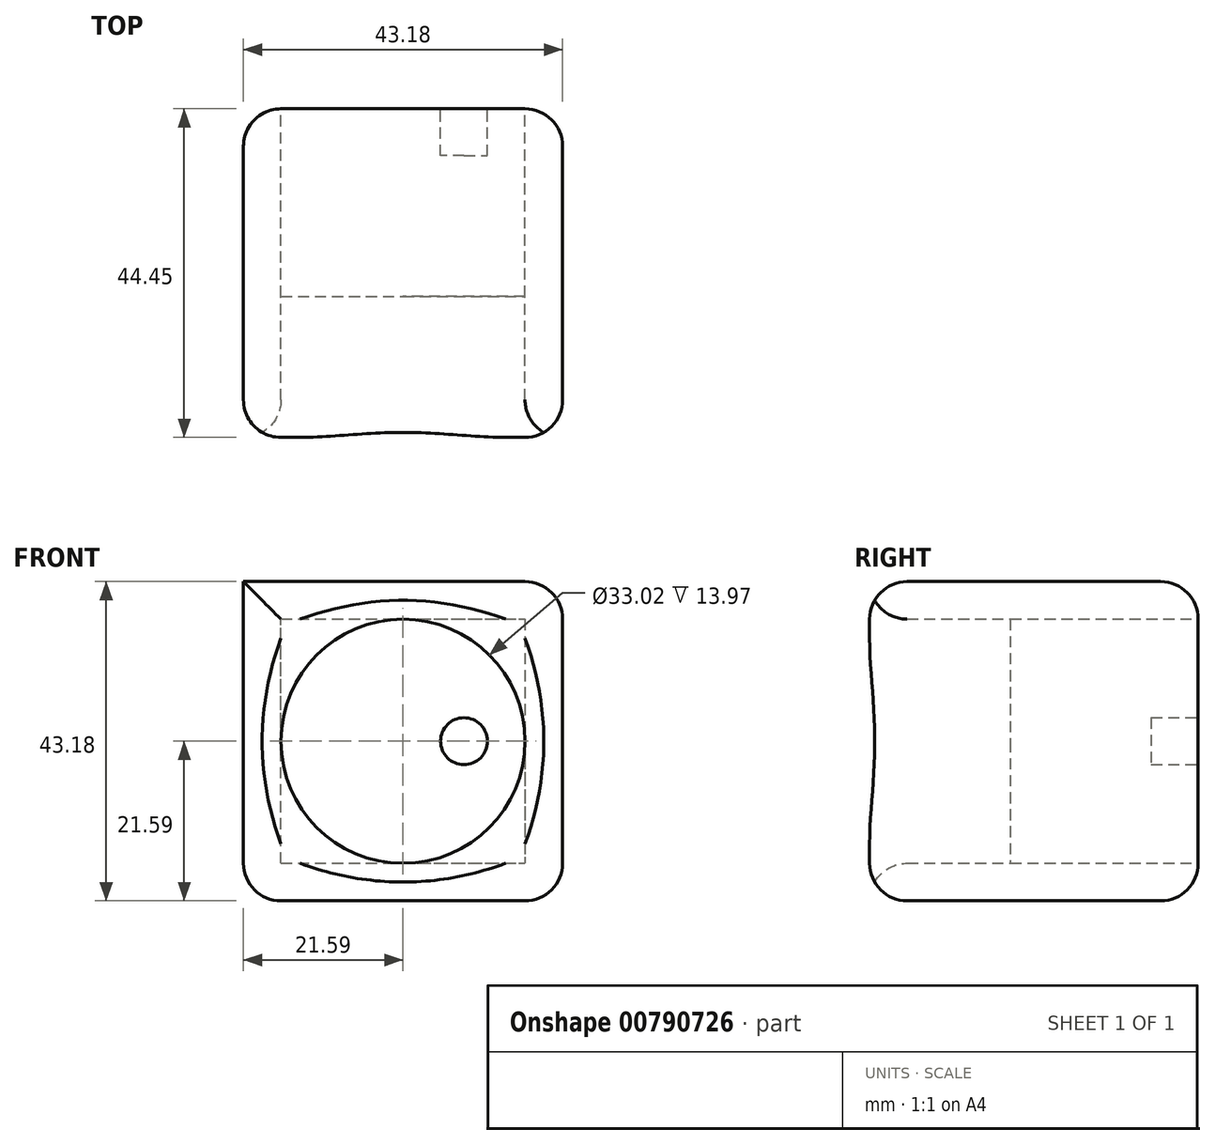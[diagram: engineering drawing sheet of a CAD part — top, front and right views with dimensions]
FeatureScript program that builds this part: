
annotation { "Feature Type Name" : "Feature", "Feature Type Description" : "" }
export const myFeature = defineFeature(function(context is Context, id is Id, definition is map)
    precondition{}
    {
        {
            var Q0;
            Q0=qCreatedBy(makeId("Front.planeOp"),FACE);
            var sketch = newSketch(context, id + "F0", { "sketchPlane" : qUnion([Q0])});
            skCircle(sketch, "E0", {"center": v(0, 0) * mm, "radius": 16.51 * mm});
            skLineSegment(sketch, "E1.top", {"start": v(0, 21.59) * mm, "end": v(-21.6, 21.59) * mm});
            skLineSegment(sketch, "E1.right", {"start": v(-21.59, 0) * mm, "end": v(-21.6, 21.59) * mm});
            skLineSegment(sketch, "E2.bottom", {"start": v(-21.6, 21.59) * mm, "end": v(21.59, 21.59) * mm});
            skLineSegment(sketch, "E2.top", {"start": v(-21.59, -21.6) * mm, "end": v(21.59, -21.6) * mm});
            skLineSegment(sketch, "E2.left", {"start": v(-21.6, 21.59) * mm, "end": v(-21.6, -21.6) * mm});
            skLineSegment(sketch, "E2.right", {"start": v(21.59, 21.59) * mm, "end": v(21.59, -21.6) * mm});
            skSolve(sketch);
        }
        {
            var Q0;
            Q0=makeQuery(id+"F0.imprint","IMPRINT",FACE,{"disambiguationData":[TD([[makeQuery(id+"F0.imprint","IMPRINT",EDGE,{"derivedFrom":sQuery(id+"F0.wireOp",EDGE,"E0")}),1.0]])]});
            extrude(context, id + "F1", {"entities" : qUnion([Q0]), "depth" : 6.35 * mm, "offsetDistance" : 25.4 * mm});
        }
        {
            var Q0;
            Q0=makeQuery(id+"F0.imprint","IMPRINT",FACE,{"disambiguationData":[TD([[makeQuery(id+"F0.imprint","IMPRINT",EDGE,{"derivedFrom":sQuery(id+"F0.wireOp",EDGE,"E0")}),-1.0]])]});
            extrude(context, id + "F2", {"entities" : qUnion([Q0]), "operationType" : NewBodyOperationType.ADD, "depth" : 44.45 * mm, "offsetDistance" : 25.4 * mm});
        }
        {
            var Q0;
            Q0=makeQuery(id+"F2.opExtrude","SWEPT_EDGE",EDGE,{"disambiguationData":[OSD([sQuery(id+"F0.wireOp",EDGE,"E2.bottom"),sQuery(id+"F0.wireOp",EDGE,"E2.right")])]});
            var Q1;
            Q1=makeQuery(id+"F2.opExtrude","SWEPT_EDGE",EDGE,{"disambiguationData":[OSD([sQuery(id+"F0.wireOp",EDGE,"E2.bottom"),sQuery(id+"F0.wireOp",EDGE,"E2.left")])]});
            var Q2;
            Q2=makeQuery(id+"F2.opExtrude","SWEPT_EDGE",EDGE,{"disambiguationData":[OSD([sQuery(id+"F0.wireOp",EDGE,"E2.top"),sQuery(id+"F0.wireOp",EDGE,"E2.left")])]});
            var Q3;
            Q3=makeQuery(id+"F2.opExtrude","SWEPT_EDGE",EDGE,{"disambiguationData":[OSD([sQuery(id+"F0.wireOp",EDGE,"E2.top"),sQuery(id+"F0.wireOp",EDGE,"E2.right")])]});
            var Q4;
            Q4=makeQuery(id+"F2.opExtrude","CAP_EDGE",EDGE,{"disambiguationData":[OSD([sQuery(id+"F0.wireOp",EDGE,"E2.top")])],"isStart":true});
            var Q5;
            Q5=makeQuery(id+"F2.opExtrude","CAP_EDGE",EDGE,{"disambiguationData":[OSD([sQuery(id+"F0.wireOp",EDGE,"E2.right")])],"isStart":true});
            var Q6;
            Q6=makeQuery(id+"F2.opExtrude","CAP_EDGE",EDGE,{"disambiguationData":[OSD([sQuery(id+"F0.wireOp",EDGE,"E2.bottom")])],"isStart":true});
            var Q7;
            Q7=makeQuery(id+"F2.opExtrude","CAP_EDGE",EDGE,{"disambiguationData":[OSD([sQuery(id+"F0.wireOp",EDGE,"E2.left")])],"isStart":true});
            var Q8;
            Q8=makeQuery(id+"F2.opExtrude","SWEPT_FACE",FACE,{"disambiguationData":[OSD([sQuery(id+"F0.wireOp",EDGE,"E2.top")])]});
            var Q9;
            Q9=makeQuery(id+"F2.opExtrude","CAP_EDGE",EDGE,{"disambiguationData":[OSD([sQuery(id+"F0.wireOp",EDGE,"E2.right")])],"isStart":false});
            var Q10;
            Q10=makeQuery(id+"F2.opExtrude","CAP_EDGE",EDGE,{"disambiguationData":[OSD([sQuery(id+"F0.wireOp",EDGE,"E2.bottom")])],"isStart":false});
            var Q11;
            Q11=makeQuery(id+"F2.opExtrude","CAP_EDGE",EDGE,{"disambiguationData":[OSD([sQuery(id+"F0.wireOp",EDGE,"E2.left")])],"isStart":false});
            var Q12;
            Q12=makeQuery(id+"F2.opExtrude","CAP_EDGE",EDGE,{"disambiguationData":[OSD([sQuery(id+"F0.wireOp",EDGE,"E0")])],"isStart":false});
            fillet(context, id + "F3", {"entities" : qUnion([Q0, Q1, Q2, Q3, Q4, Q5, Q6, Q7, Q8, Q9, Q10, Q11, Q12]), "radius" : 5.08 * mm, "tangentPropagation" : true, "allowEdgeOverflow" : false});
        }
        {
            var Q0;
            {var subQ0=sQuery(id+"F0.wireOp",EDGE,"E0");Q0=makeQuery(id+"F2.boolean.opBoolean","MERGE",FACE,{"derivedFrom":[makeQuery(id+"F1.opExtrude","CAP_FACE",FACE,{"disambiguationData":[OSD([subQ0])],"isStart":true}),makeQuery(id+"F2.opExtrude","CAP_FACE",FACE,{"disambiguationData":[OSD([subQ0,sQuery(id+"F0.wireOp",EDGE,"E2.bottom"),sQuery(id+"F0.wireOp",EDGE,"E2.top"),sQuery(id+"F0.wireOp",EDGE,"E2.left"),sQuery(id+"F0.wireOp",EDGE,"E2.right")])],"isStart":true})]});}
            var sketch = newSketch(context, id + "F4", { "sketchPlane" : qUnion([Q0])});
            skCircle(sketch, "E3", {"center": v(8.26, 0) * mm, "radius": 3.18 * mm});
            skCircle(sketch, "E4.MirrorC", {"center": v(-8.25, 0) * mm, "radius": 3.18 * mm});
            skPoint(sketch, "E5.orphan", {"position": v(0, 0) * mm});
            skPoint(sketch, "E6.orphan", {"position": v(0, -16.51) * mm});
            skPoint(sketch, "E7.start.orphan", {"position": v(0, 16.5) * mm});
            skPoint(sketch, "E8.end.orphan", {"position": v(16.51, 0) * mm});
            skSolve(sketch);
        }
        {
            var Q0;
            Q0=makeQuery(id+"F4.imprint","IMPRINT",FACE,{"disambiguationData":[TD([[makeQuery(id+"F4.imprint","IMPRINT",EDGE,{"derivedFrom":sQuery(id+"F4.wireOp",EDGE,"E4.MirrorC")}),-1.0]])]});
            var Q1;
            Q1=makeQuery(id+"F4.imprint","IMPRINT",FACE,{"disambiguationData":[TD([[makeQuery(id+"F4.imprint","IMPRINT",EDGE,{"derivedFrom":sQuery(id+"F4.wireOp",EDGE,"E3")}),1.0]])]});
            extrude(context, id + "F5", {"entities" : qUnion([Q0, Q1]), "operationType" : NewBodyOperationType.REMOVE, "oppositeDirection" : true, "depth" : 25.4 * mm, "offsetDistance" : 25.4 * mm});
        }
    });
